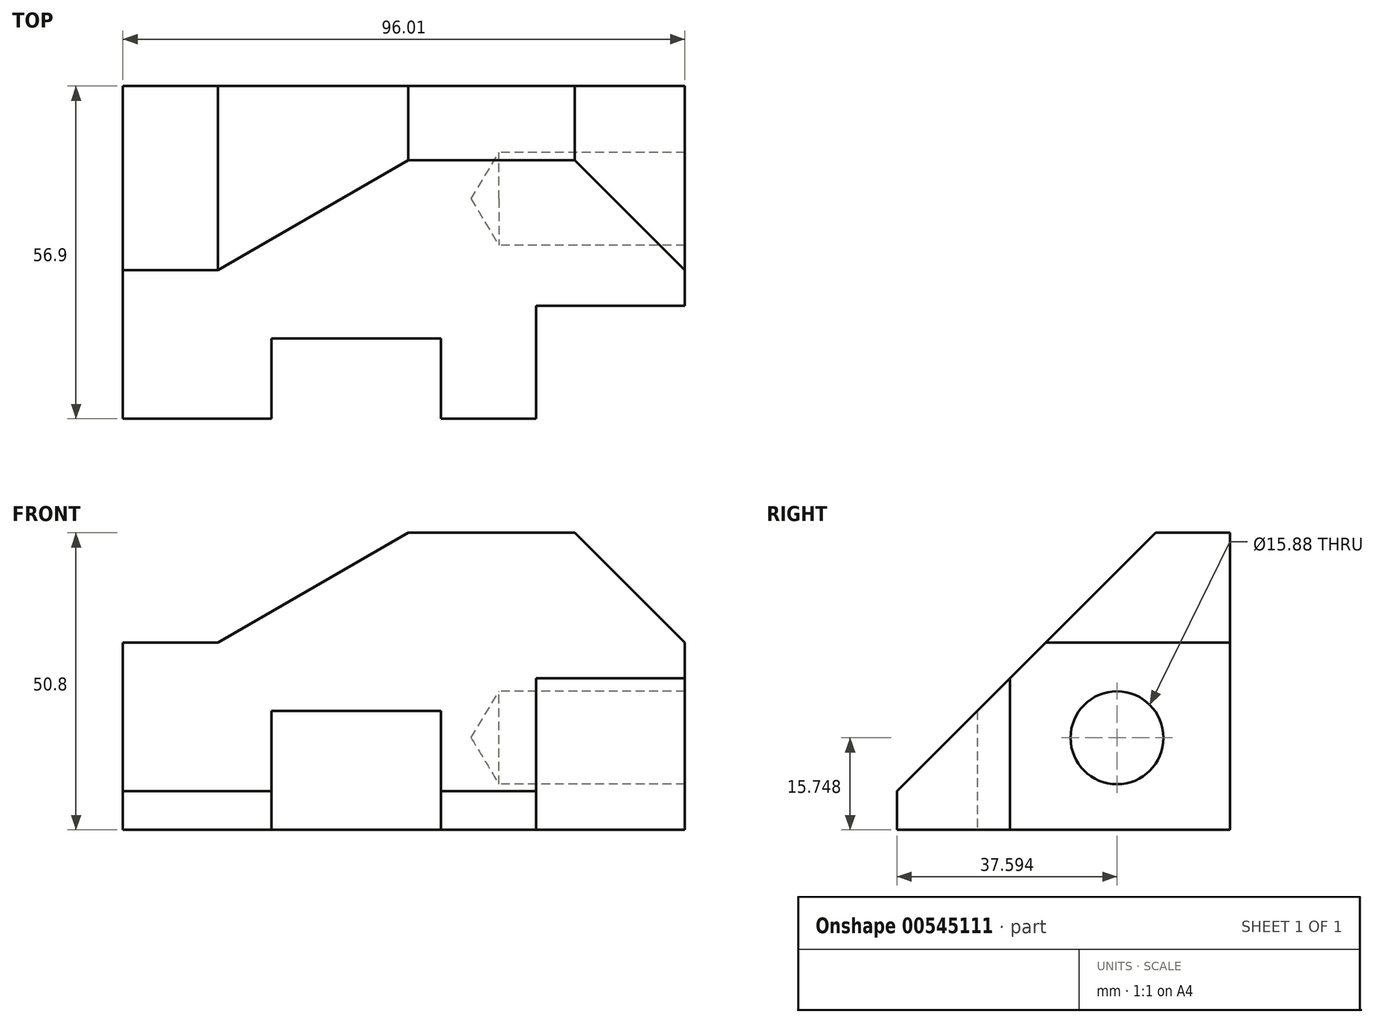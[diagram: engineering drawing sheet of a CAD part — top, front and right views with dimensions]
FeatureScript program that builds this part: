
annotation { "Feature Type Name" : "Feature", "Feature Type Description" : "" }
export const myFeature = defineFeature(function(context is Context, id is Id, definition is map)
    precondition{}
    {
        {
            var Q0;
            Q0=qCreatedBy(makeId("Right.planeOp"),FACE);
            var sketch = newSketch(context, id + "F0", { "sketchPlane" : qUnion([Q0])});
            skLineSegment(sketch, "E0", {"start": v(55.83, 23.2) * mm, "end": v(55.83, -27.6) * mm});
            skLineSegment(sketch, "E1", {"start": v(55.83, -27.6) * mm, "end": v(-1.07, -27.6) * mm});
            skLineSegment(sketch, "E2", {"start": v(55.83, 23.2) * mm, "end": v(43.13, 23.2) * mm});
            skLineSegment(sketch, "E3", {"start": v(43.13, 23.2) * mm, "end": v(-1.07, -21) * mm});
            skLineSegment(sketch, "E4", {"start": v(-1.07, -27.6) * mm, "end": v(-1.07, -21) * mm});
            skSolve(sketch);
        }
        {
            var Q0;
            Q0=makeQuery(id+"F0.imprint","IMPRINT",FACE,{"disambiguationData":[TD([[makeQuery(id+"F0.imprint","IMPRINT",EDGE,{"derivedFrom":sQuery(id+"F0.wireOp",EDGE,"E0")}),-1.0]])]});
            extrude(context, id + "F1", {"entities" : qUnion([Q0]), "depth" : 96.01 * mm, "offsetDistance" : 25.4 * mm});
        }
        {
            var Q0;
            Q0=makeQuery(id+"F1.opExtrude","CAP_FACE",FACE,{"disambiguationData":[OSD([sQuery(id+"F0.wireOp",EDGE,"E0"),sQuery(id+"F0.wireOp",EDGE,"E1"),sQuery(id+"F0.wireOp",EDGE,"E2"),sQuery(id+"F0.wireOp",EDGE,"E3"),sQuery(id+"F0.wireOp",EDGE,"E4")])],"isStart":false});
            var sketch = newSketch(context, id + "F2", { "sketchPlane" : qUnion([Q0])});
            skPoint(sketch, "E5", {"position": v(36.52, -11.86) * mm});
            skSolve(sketch);
        }
        {
            var Q0;
            Q0=sQuery(id+"F2.wireOp",VERTEX,"E5");
            var Q1;
            Q1=makeQuery(id+"F1.opExtrude","SWEPT_BODY",BODY,{"disambiguationData":[OSD([sQuery(id+"F0.wireOp",EDGE,"E0"),sQuery(id+"F0.wireOp",EDGE,"E1"),sQuery(id+"F0.wireOp",EDGE,"E2"),sQuery(id+"F0.wireOp",EDGE,"E3"),sQuery(id+"F0.wireOp",EDGE,"E4")])]});
            hole(context, id + "F3", {"style" : HoleStyle.SIMPLE, "endStyle" : HoleEndStyle.BLIND, "holeDiameter" : 15.88 * mm, "holeDepth" : 31.75 * mm, "isTappedThrough" : true, "tappedDepth" : 12.7 * mm, "tapClearance" : 3, "startFromSketch" : true, "locations" : qUnion([Q0]), "scope" : qUnion([Q1])});
        }
        {
            var Q0;
            Q0=makeQuery(id+"F1.opExtrude","SWEPT_FACE",FACE,{"disambiguationData":[OSD([sQuery(id+"F0.wireOp",EDGE,"E0")])]});
            var sketch = newSketch(context, id + "F4", { "sketchPlane" : qUnion([Q0])});
            skLineSegment(sketch, "E6", {"start": v(-77.22, 23.2) * mm, "end": v(-96.01, 4.4) * mm});
            skPoint(sketch, "E7.start.orphan", {"position": v(-77.22, 7.31) * mm});
            skPoint(sketch, "E8.end.orphan", {"position": v(-77.22, 4.4) * mm});
            skSolve(sketch);
        }
        {
            var Q0;
            {var subQ0=sQuery(id+"F4.wireOp",EDGE,"E6");Q0=makeQuery(id+"F4.imprint","IMPRINT",FACE,{"disambiguationData":[TD([[makeQuery(id+"F4.imprint","IMPRINT",EDGE,{"derivedFrom":subQ0}),-1.0]])]});}
            extrude(context, id + "F5", {"entities" : qUnion([Q0]), "operationType" : NewBodyOperationType.REMOVE, "endBound" : BoundingType.THROUGH_ALL, "oppositeDirection" : true, "depth" : 25.4 * mm, "offsetDistance" : 25.4 * mm});
        }
        {
            var Q0;
            Q0=makeQuery(id+"F1.opExtrude","SWEPT_FACE",FACE,{"disambiguationData":[OSD([sQuery(id+"F0.wireOp",EDGE,"E1")])]});
            var sketch = newSketch(context, id + "F6", { "sketchPlane" : qUnion([Q0])});
            skLineSegment(sketch, "E9", {"start": v(25.4, 1.07) * mm, "end": v(25.4, -12.65) * mm});
            skLineSegment(sketch, "E10.0", {"start": v(54.36, 1.07) * mm, "end": v(54.36, -12.65) * mm});
            skLineSegment(sketch, "E11", {"start": v(54.36, -12.65) * mm, "end": v(25.4, -12.65) * mm});
            skLineSegment(sketch, "E12", {"start": v(70.61, 1.07) * mm, "end": v(70.61, -18.24) * mm});
            skLineSegment(sketch, "E13", {"start": v(70.61, -18.24) * mm, "end": v(96.01, -18.24) * mm});
            skSolve(sketch);
        }
        {
            var Q0;
            {var subQ0=sQuery(id+"F6.wireOp",EDGE,"E9");Q0=makeQuery(id+"F6.imprint","IMPRINT",FACE,{"disambiguationData":[TD([[makeQuery(id+"F6.imprint","IMPRINT",EDGE,{"derivedFrom":subQ0}),1.0]])]});}
            var Q1;
            {var subQ0=sQuery(id+"F6.wireOp",EDGE,"E12");Q1=makeQuery(id+"F6.imprint","IMPRINT",FACE,{"disambiguationData":[TD([[makeQuery(id+"F6.imprint","IMPRINT",EDGE,{"derivedFrom":subQ0}),1.0]])]});}
            extrude(context, id + "F7", {"entities" : qUnion([Q0, Q1]), "operationType" : NewBodyOperationType.REMOVE, "endBound" : BoundingType.THROUGH_ALL, "oppositeDirection" : true, "depth" : 25.4 * mm, "offsetDistance" : 25.4 * mm});
        }
        {
            var Q0;
            Q0=makeQuery(id+"F1.opExtrude","SWEPT_FACE",FACE,{"disambiguationData":[OSD([sQuery(id+"F0.wireOp",EDGE,"E0")])]});
            var sketch = newSketch(context, id + "F8", { "sketchPlane" : qUnion([Q0])});
            skLineSegment(sketch, "E14", {"start": v(0, 4.4) * mm, "end": v(-16.21, 4.4) * mm});
            skLineSegment(sketch, "E15", {"start": v(-48.77, 23.2) * mm, "end": v(-16.21, 4.4) * mm});
            skSolve(sketch);
        }
        {
            var Q0;
            {var subQ0=sQuery(id+"F8.wireOp",EDGE,"E14");Q0=makeQuery(id+"F8.imprint","IMPRINT",FACE,{"disambiguationData":[TD([[makeQuery(id+"F8.imprint","IMPRINT",EDGE,{"derivedFrom":subQ0}),-1.0]])]});}
            extrude(context, id + "F9", {"entities" : qUnion([Q0]), "operationType" : NewBodyOperationType.REMOVE, "endBound" : BoundingType.THROUGH_ALL, "oppositeDirection" : true, "depth" : 25.4 * mm, "offsetDistance" : 25.4 * mm});
        }
    });
